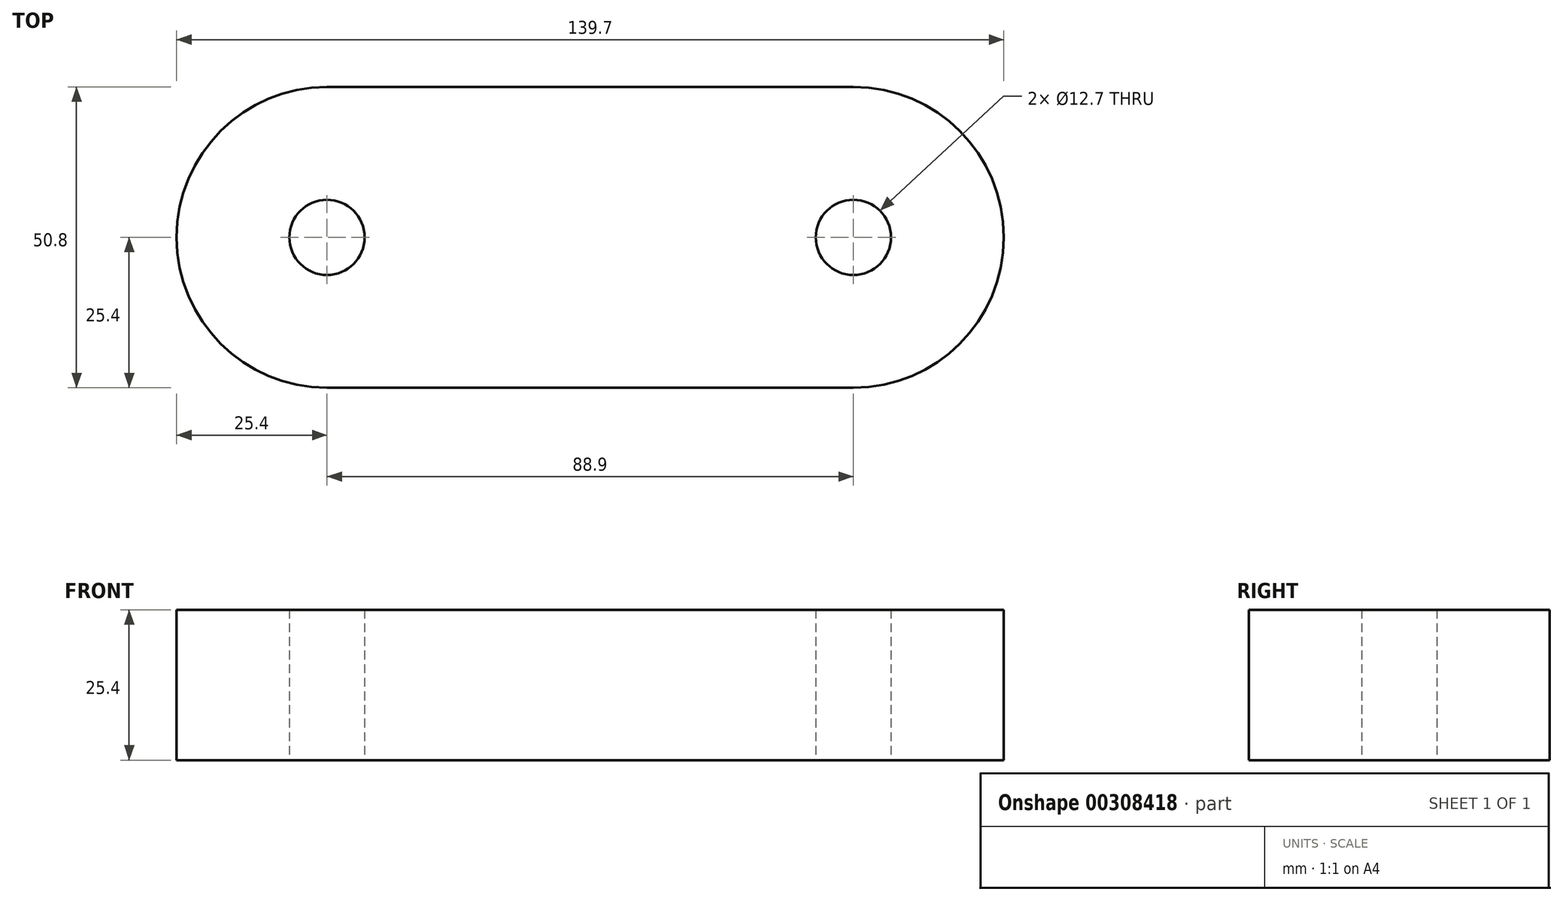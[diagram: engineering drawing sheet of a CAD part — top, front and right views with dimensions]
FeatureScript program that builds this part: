
annotation { "Feature Type Name" : "Feature", "Feature Type Description" : "" }
export const myFeature = defineFeature(function(context is Context, id is Id, definition is map)
    precondition{}
    {
        {
            var Q0;
            Q0=qCreatedBy(makeId("Top.planeOp"),FACE);
            var sketch = newSketch(context, id + "F0", { "sketchPlane" : qUnion([Q0])});
            skLineSegment(sketch, "E0", {"start": v(0, -25.4) * mm, "end": v(88.9, -25.4) * mm});
            skLineSegment(sketch, "E1", {"start": v(88.9, 25.4) * mm, "end": v(0, 25.4) * mm});
            skArc(sketch, "E2", {"start": v(0, 25.4) * mm, "mid": v(-25.4, 0) * mm, "end": v(0, -25.4) * mm});
            skArc(sketch, "E3", {"start": v(88.9, -25.4) * mm, "mid": v(114.3, 0) * mm, "end": v(88.9, 25.4) * mm});
            skCircle(sketch, "E4", {"center": v(0, 0) * mm, "radius": 6.35 * mm});
            skCircle(sketch, "E5", {"center": v(88.9, 0) * mm, "radius": 6.35 * mm});
            skSolve(sketch);
        }
        {
            var Q0;
            Q0 = qSketchRegion(id + "F0", true);
            extrude(context, id + "F1", {"entities" : qUnion([Q0]), "depth" : 25.4 * mm});
        }
    });
